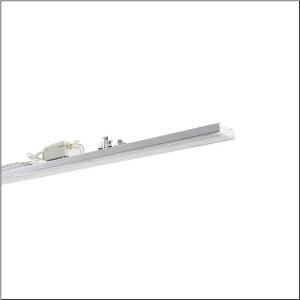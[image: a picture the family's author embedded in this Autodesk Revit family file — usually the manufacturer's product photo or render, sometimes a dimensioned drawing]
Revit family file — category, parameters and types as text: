
# Revit family: licross_r__21_recessed_mo_52tl12dn4axgd_376d
name_source: partatom
category: Lighting Fixtures
units: mm (PartAtom-declared; Revit-internal decimal feet)

## family parameters
Cut with Voids When Loaded = No
Host = Face
Light Source = No
Part Type = Normal
Room Calculation Point = No
Round Connector Dimension = Use Diameter
Shared = No

## types (1)
- --- (1 x LED, 1540 lm, 9.7 W, 4000K)
    Apparent Load = 10 VA
    CIE Flux Codes = 72 92 99 100 100
    Color Rendering = 80
    Color Temperature = 4000K
    Default Elevation = 1800 mm
    Description = Licross® 21 Recessed MO, luminaire insert, of sheet steel, galvanised, coil coated, white, length: 1.500mm, width: 66mm, height: 67mm, LED rated luminous flux: 10.280lm, light colour: 840, control gear: DALI 2, with plug, 6-pole, with phase selection, mains connection: 220..240V, AC/DC, 0/50..60Hz, rated input power: 58W, without changeover relay, for emergency light function, for central battery installations according to DIN EN 60598-2-22, halogen-free wiring, primary optical cover: cover, of PMMA, light emission: direct distribution, primary light characteristic: symmetric, protection rating (complete): IP40, insulation class (complete): insulation class I (protective earthing), certification: CE, ENEC, VDE, UKCA, protection symbol: D if used in an environment without relevant dust loads with corresponding accessories, impact resistance: IK06, permissible ambient temperature for indoor applications: -25..+35°C, standard: EN 60598-2-22, corresponds to IFS (International Featured Standards) requirements for safety and quality in the food industry, reducing of maximum allowable ambient temperature of 5°C with ceiling mounting, LABS conformity tested according to VDMA 24364:2018-05, packaging unit: 1 piece
    Height = 58 mm
    Lamp = 1 x LED
    Lamp Light Flux = 1540 lm
    Lamp Power = 9.7 W
    Lamp count = 1
    Length = 1500 mm
    Luminous efficacy = 159 lm/W
    Manufacturer = Siteco
    ModVariant = No
    Model = 52TL12DN4AXGD
    Mounting Place = Ceiling
    Mounting Type = Pendant
    Number of Poles = 1
    OnlyDefault = Yes
    Power Factor = 1
    Product Name = Licross® 21 Recessed MO
    Product group = luminaire insert
    ProductGroupID = 901
    Protection Class = Protection class I
    Protection Degree = IP 40
    RLX_Detail_Level = 1
    RLX_Emergency_Light_Flux = 0 lm
    RLX_Emergency_Type = 0
    RLX_Emergency_Type_DB = No
    RlxData = <blob elided: 25101 chars, md5=6010a99f>
    Socket = socket
    Standby Power = 0 W
    System Light Flux = 1540 lm
    System Power = 10 W
    Type Comments = : DC mode (central or group accumulator) initial emergency light level
    Type Image = l_1296930.jpg
    URL = http://relux.com
    VarID = @adj_043189
    Voltage = 0 V
    Weight = 0.00 kg
    Width = 66 mm

## geometry (parser evidence)
native form markers: Blend x4, Sweep x10
no freeform markers — native parametric forms only
